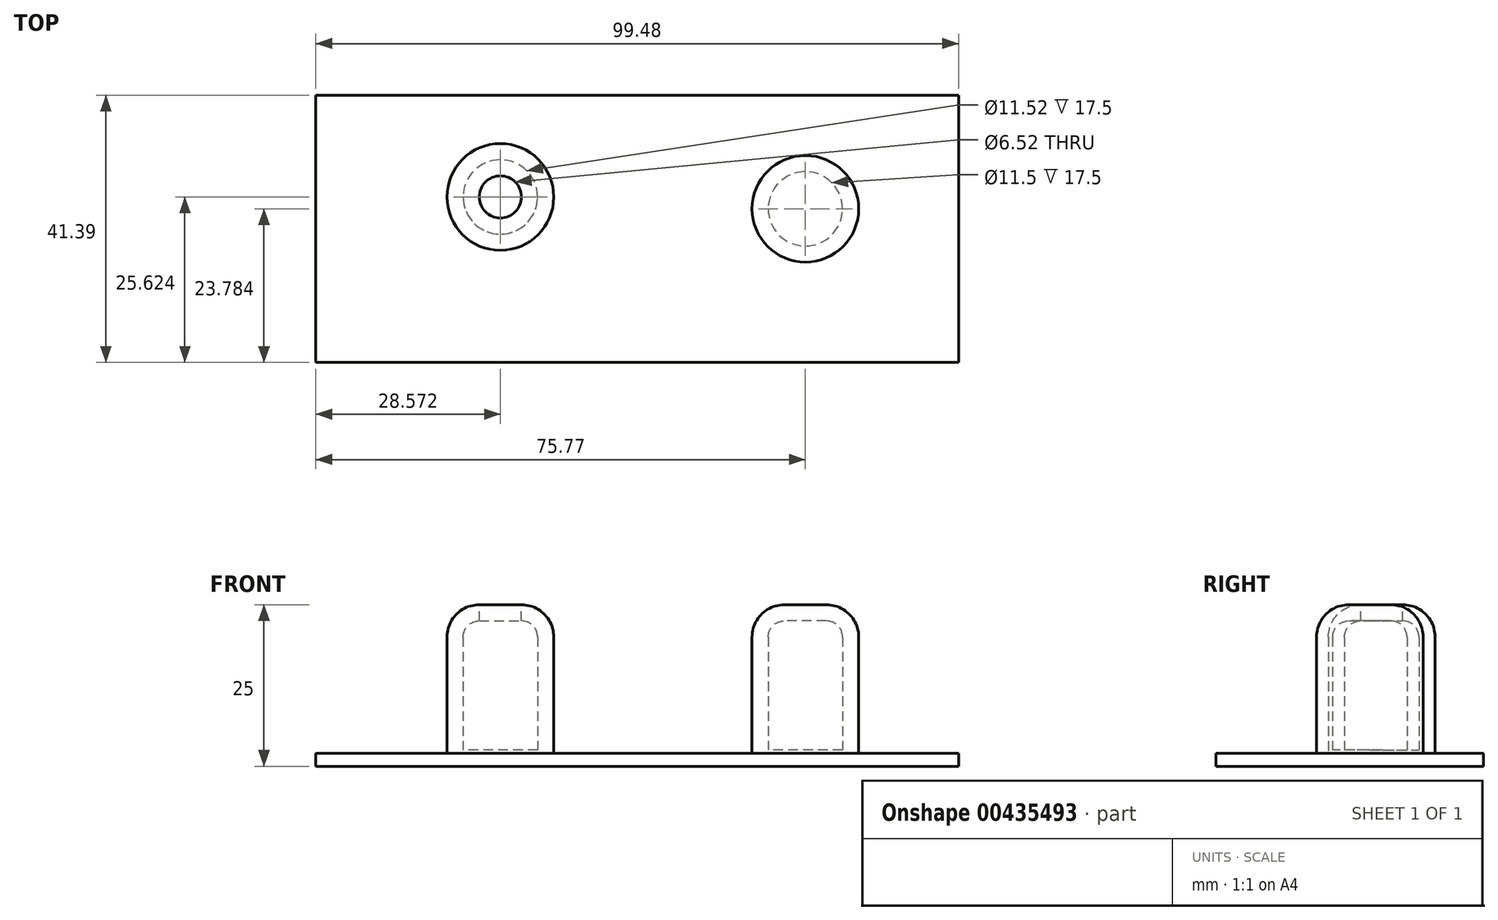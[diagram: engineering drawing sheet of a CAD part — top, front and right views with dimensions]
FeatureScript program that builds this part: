
annotation { "Feature Type Name" : "Feature", "Feature Type Description" : "" }
export const myFeature = defineFeature(function(context is Context, id is Id, definition is map)
    precondition{}
    {
        {
            var Q0;
            Q0=qCreatedBy(makeId("Top.planeOp"),FACE);
            var sketch = newSketch(context, id + "F0", { "sketchPlane" : qUnion([Q0])});
            skLineSegment(sketch, "E0.bottom", {"start": v(-49.06, 52.84) * mm, "end": v(50.42, 52.84) * mm});
            skLineSegment(sketch, "E0.top", {"start": v(-49.06, 11.45) * mm, "end": v(50.42, 11.45) * mm});
            skLineSegment(sketch, "E0.left", {"start": v(-49.06, 52.84) * mm, "end": v(-49.06, 11.45) * mm});
            skLineSegment(sketch, "E0.right", {"start": v(50.42, 52.84) * mm, "end": v(50.42, 11.45) * mm});
            skSolve(sketch);
        }
        {
            var Q0;
            Q0=makeQuery(id+"F0.imprint","IMPRINT",FACE,{"disambiguationData":[TD([[makeQuery(id+"F0.imprint","IMPRINT",EDGE,{"derivedFrom":sQuery(id+"F0.wireOp",EDGE,"E0.bottom")}),-1.0]])]});
            extrude(context, id + "F1", {"entities" : qUnion([Q0]), "depth" : 2 * mm});
        }
        {
            var Q0;
            Q0=qCreatedBy(makeId("Top.planeOp"),FACE);
            var sketch = newSketch(context, id + "F2", { "sketchPlane" : qUnion([Q0])});
            skCircle(sketch, "E1", {"center": v(-20.49, 37.07) * mm, "radius": 8.26 * mm});
            skCircle(sketch, "E2", {"center": v(26.7, 35.23) * mm, "radius": 8.25 * mm});
            skSolve(sketch);
        }
        {
            var Q0;
            Q0 = qSketchRegion(id + "F2", true);
            extrude(context, id + "F3", {"entities" : qUnion([Q0]), "operationType" : NewBodyOperationType.ADD, "depth" : 25 * mm});
        }
        {
            var Q0;
            Q0=makeQuery(id+"F3.opExtrude","CAP_EDGE",EDGE,{"disambiguationData":[OSD([sQuery(id+"F2.wireOp",EDGE,"E1")])],"isStart":false});
            fillet(context, id + "F4", {"entities" : qUnion([Q0]), "radius" : 5 * mm, "tangentPropagation" : true, "allowEdgeOverflow" : false});
        }
        {
            var Q0;
            Q0=makeQuery(id+"F3.opExtrude","CAP_FACE",FACE,{"disambiguationData":[OSD([sQuery(id+"F2.wireOp",EDGE,"E2")])],"isStart":false});
            fillet(context, id + "F5", {"entities" : qUnion([Q0]), "radius" : 5 * mm, "tangentPropagation" : true, "allowEdgeOverflow" : false});
        }
        {
            var Q0;
            Q0=makeQuery(id+"F3.opExtrude","CAP_FACE",FACE,{"disambiguationData":[OSD([sQuery(id+"F2.wireOp",EDGE,"E1")])],"isStart":false});
            shell(context, id + "F6", {"entities" : qUnion([Q0]), "thickness" : 2.5 * mm});
        }
    });
